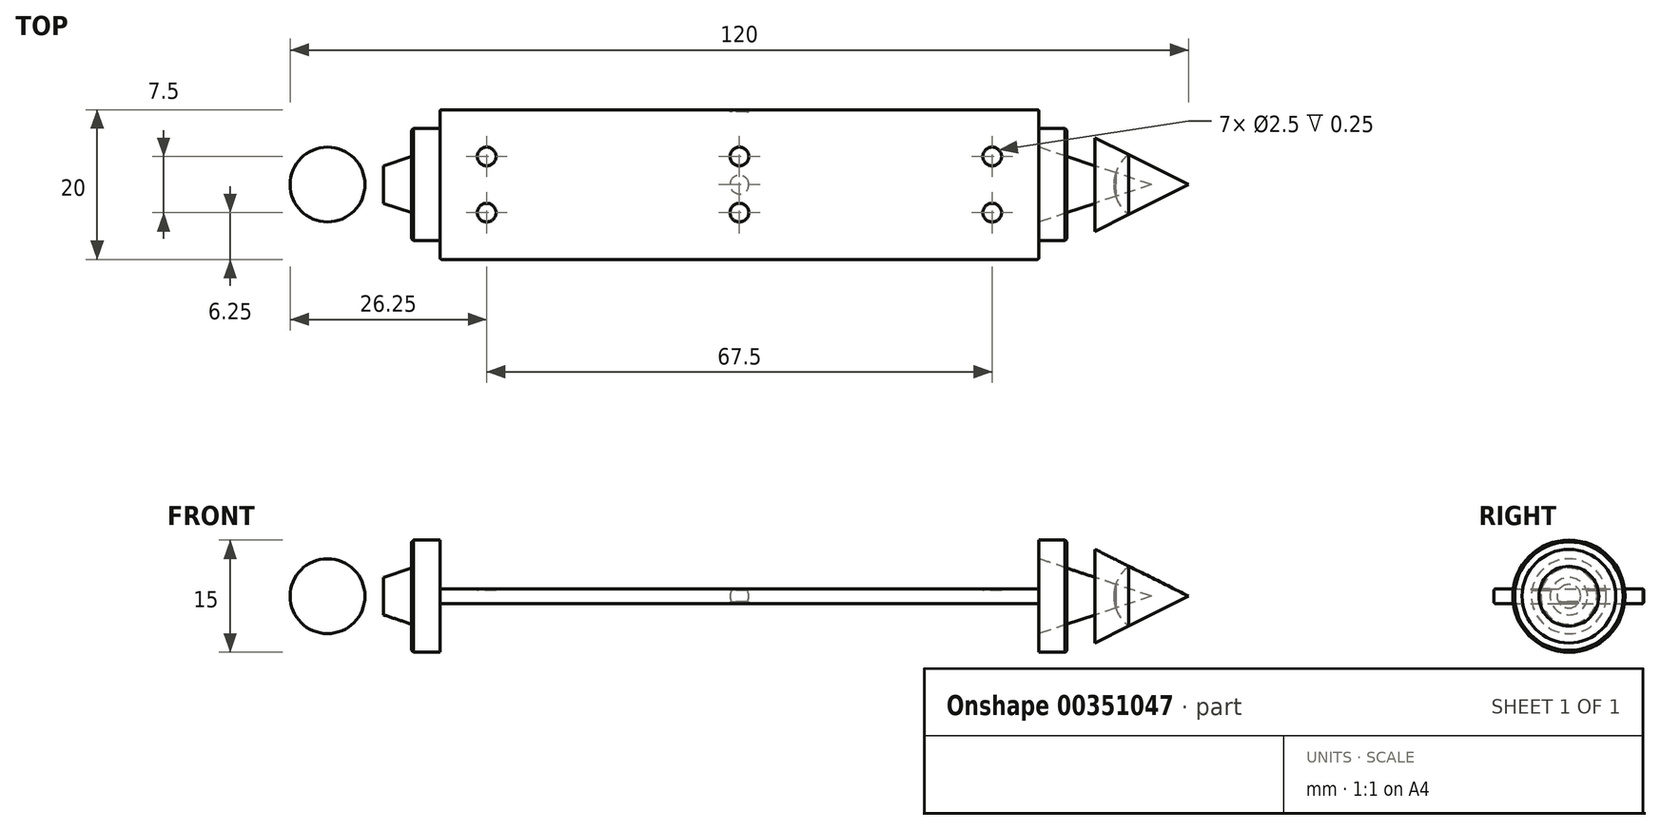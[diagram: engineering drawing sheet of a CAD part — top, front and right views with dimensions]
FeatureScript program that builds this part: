
annotation { "Feature Type Name" : "Feature", "Feature Type Description" : "" }
export const myFeature = defineFeature(function(context is Context, id is Id, definition is map)
    precondition{}
    {
        {
            assignVariable(context, id + "F0", {"name" : "H", "anyValue" : 2});
        }
        {
            assignVariable(context, id + "F1", {"name" : "E", "anyValue" : .25});
        }
        {
            var Q0;
            Q0=qCreatedBy(makeId("Top.planeOp"),FACE);
            var sketch = newSketch(context, id + "F2", { "sketchPlane" : qUnion([Q0])});
            skLineSegment(sketch, "E0.bottom", {"start": v(0, 0) * mm, "end": v(-40, 0) * mm});
            skLineSegment(sketch, "E0.top", {"start": v(0, 10) * mm, "end": v(-40, 10) * mm});
            skLineSegment(sketch, "E0.left", {"start": v(0, 0) * mm, "end": v(0, 10) * mm});
            skLineSegment(sketch, "E0.right", {"start": v(-40, 0) * mm, "end": v(-40, 10) * mm});
            skLineSegment(sketch, "E1.MirrorCS", {"start": v(0, 10) * mm, "end": v(40, 10) * mm});
            skLineSegment(sketch, "E2.MirrorCS", {"start": v(40, 0) * mm, "end": v(40, 10) * mm});
            skLineSegment(sketch, "E3.MirrorCS", {"start": v(0, 0) * mm, "end": v(40, 0) * mm});
            skLineSegment(sketch, "E4.MirrorCS", {"start": v(0, -10) * mm, "end": v(-40, -10) * mm});
            skLineSegment(sketch, "E5.MirrorCS", {"start": v(0, -10) * mm, "end": v(40, -10) * mm});
            skLineSegment(sketch, "E6.MirrorCS", {"start": v(-40, 0) * mm, "end": v(-40, -10) * mm});
            skLineSegment(sketch, "E7.MirrorCS", {"start": v(40, 0) * mm, "end": v(40, -10) * mm});
            skLineSegment(sketch, "E8", {"start": v(40, 0) * mm, "end": v(60, 0) * mm});
            skPoint(sketch, "E9", {"position": v(40, 5) * mm});
            skPoint(sketch, "E10", {"position": v(40, -5) * mm});
            skPoint(sketch, "E11", {"position": v(50, 0) * mm});
            skPoint(sketch, "E12", {"position": v(55, 0) * mm});
            skCircle(sketch, "E13", {"center": v(55, 0) * mm, "radius": 5 * mm});
            skLineSegment(sketch, "E14", {"start": v(55, 0) * mm, "end": v(40, 5) * mm});
            skLineSegment(sketch, "E15", {"start": v(40, -5) * mm, "end": v(55, 0) * mm});
            skLineSegment(sketch, "E16", {"start": v(60, 0) * mm, "end": v(40, 10) * mm});
            skLineSegment(sketch, "E17", {"start": v(60, 0) * mm, "end": v(40, -10) * mm});
            skCircle(sketch, "E18.MirrorC", {"center": v(-55, 0) * mm, "radius": 5 * mm});
            skLineSegment(sketch, "E19.MirrorCS", {"start": v(-55, 0) * mm, "end": v(-40, 5) * mm});
            skLineSegment(sketch, "E20.MirrorCS", {"start": v(-60, 0) * mm, "end": v(-40, 10) * mm});
            skLineSegment(sketch, "E21.MirrorCS", {"start": v(-40, 0) * mm, "end": v(-60, 0) * mm});
            skPoint(sketch, "E22", {"position": v(40, 7.5) * mm});
            skPoint(sketch, "E23", {"position": v(40, -7.5) * mm});
            skPoint(sketch, "E24.oppositeSnap0", {"position": v(47.5, 2.5) * mm});
            skLineSegment(sketch, "E24.bottom", {"start": v(40, 7.5) * mm, "end": v(47.5, 7.5) * mm});
            skLineSegment(sketch, "E24.top", {"start": v(40, -7.5) * mm, "end": v(47.5, -7.5) * mm});
            skLineSegment(sketch, "E24.left", {"start": v(40, 7.5) * mm, "end": v(40, -7.5) * mm});
            skLineSegment(sketch, "E24.right", {"start": v(47.5, 7.5) * mm, "end": v(47.5, -7.5) * mm});
            skLineSegment(sketch, "E25.MirrorCS", {"start": v(-40, 7.5) * mm, "end": v(-47.5, 7.5) * mm});
            skLineSegment(sketch, "E26.MirrorCS", {"start": v(-47.5, 7.5) * mm, "end": v(-47.5, -7.5) * mm});
            skLineSegment(sketch, "E27", {"start": v(43.75, 7.5) * mm, "end": v(43.75, -7.5) * mm});
            skLineSegment(sketch, "E28.MirrorCS", {"start": v(-43.75, 7.5) * mm, "end": v(-43.75, -7.5) * mm});
            skSolve(sketch);
        }
        {
            var Q0;
            Q0=makeQuery(id+"F2.imprint","IMPRINT",FACE,{"disambiguationData":[TD([[makeQuery(id+"F2.imprint","IMPRINT",EDGE,{"derivedFrom":sQuery(id+"F2.wireOp",EDGE,"E0.bottom")}),-1.0]])]});
            var Q1;
            Q1=makeQuery(id+"F2.imprint","IMPRINT",FACE,{"disambiguationData":[TD([[makeQuery(id+"F2.imprint","IMPRINT",EDGE,{"derivedFrom":sQuery(id+"F2.wireOp",EDGE,"E0.left")}),-1.0]])]});
            var Q2;
            Q2=makeQuery(id+"F2.imprint","IMPRINT",FACE,{"disambiguationData":[TD([[makeQuery(id+"F2.imprint","IMPRINT",EDGE,{"derivedFrom":sQuery(id+"F2.wireOp",EDGE,"E0.bottom")}),1.0]])]});
            extrude(context, id + "F3", {"entities" : qUnion([Q0, Q1, Q2]), "depth" : (getVariable(context, 'H') / 2) * mm, "hasSecondDirection" : true, "secondDirectionOppositeDirection" : true, "secondDirectionDepth" : (getVariable(context, 'H') / 2) * mm});
        }
        {
            var Q0;
            Q0=makeQuery(id+"F3.opExtrude","CAP_EDGE",EDGE,{"disambiguationData":[OSD([sQuery(id+"F2.wireOp",EDGE,"E4.MirrorCS"),sQuery(id+"F2.wireOp",EDGE,"E5.MirrorCS")])],"isStart":false});
            var Q1;
            Q1=makeQuery(id+"F3.opExtrude","CAP_EDGE",EDGE,{"disambiguationData":[OSD([sQuery(id+"F2.wireOp",EDGE,"E0.top"),sQuery(id+"F2.wireOp",EDGE,"E1.MirrorCS")])],"isStart":false});
            var Q2;
            Q2=makeQuery(id+"F3.opExtrude","CAP_EDGE",EDGE,{"disambiguationData":[OSD([sQuery(id+"F2.wireOp",EDGE,"E4.MirrorCS"),sQuery(id+"F2.wireOp",EDGE,"E5.MirrorCS")])],"isStart":true});
            var Q3;
            Q3=makeQuery(id+"F3.opExtrude","CAP_EDGE",EDGE,{"disambiguationData":[OSD([sQuery(id+"F2.wireOp",EDGE,"E0.top"),sQuery(id+"F2.wireOp",EDGE,"E1.MirrorCS")])],"isStart":true});
            var Q4;
            Q4=makeQuery(id+"F3.opExtrude","CAP_EDGE",EDGE,{"disambiguationData":[OSD([sQuery(id+"F2.wireOp",EDGE,"E0.right"),sQuery(id+"F2.wireOp",EDGE,"E6.MirrorCS")])],"isStart":true});
            var Q5;
            Q5=makeQuery(id+"F3.opExtrude","SWEPT_EDGE",EDGE,{"disambiguationData":[OSD([sQuery(id+"F2.wireOp",EDGE,"E0.top"),sQuery(id+"F2.wireOp",EDGE,"E0.right")])]});
            var Q6;
            Q6=makeQuery(id+"F3.opExtrude","SWEPT_FACE",FACE,{"disambiguationData":[OSD([sQuery(id+"F2.wireOp",EDGE,"E0.right"),sQuery(id+"F2.wireOp",EDGE,"E6.MirrorCS")])]});
            var Q7;
            Q7=makeQuery(id+"F3.opExtrude","SWEPT_FACE",FACE,{"disambiguationData":[OSD([sQuery(id+"F2.wireOp",EDGE,"E2.MirrorCS"),sQuery(id+"F2.wireOp",EDGE,"E7.MirrorCS")])]});
            fillet(context, id + "F4", {"entities" : qUnion([Q0, Q1, Q2, Q3, Q4, Q5, Q6, Q7]), "radius" : (getVariable(context, 'E')) * mm, "tangentPropagation" : true, "allowEdgeOverflow" : false});
        }
        {
            var Q0;
            Q0=makeQuery(id+"F3.opExtrude","CAP_FACE",FACE,{"disambiguationData":[OSD([sQuery(id+"F2.wireOp",EDGE,"E0.top"),sQuery(id+"F2.wireOp",EDGE,"E0.right"),sQuery(id+"F2.wireOp",EDGE,"E1.MirrorCS"),sQuery(id+"F2.wireOp",EDGE,"E2.MirrorCS"),sQuery(id+"F2.wireOp",EDGE,"E4.MirrorCS"),sQuery(id+"F2.wireOp",EDGE,"E5.MirrorCS"),sQuery(id+"F2.wireOp",EDGE,"E6.MirrorCS"),sQuery(id+"F2.wireOp",EDGE,"E7.MirrorCS")])],"isStart":false});
            var sketch = newSketch(context, id + "F5", { "sketchPlane" : qUnion([Q0])});
            skLineSegment(sketch, "E29.bottom", {"start": v(-33.75, 3.75) * mm, "end": v(33.75, 3.75) * mm});
            skLineSegment(sketch, "E29.top", {"start": v(-33.75, -3.75) * mm, "end": v(33.75, -3.75) * mm});
            skLineSegment(sketch, "E29.left", {"start": v(-33.75, 3.75) * mm, "end": v(-33.75, -3.75) * mm});
            skLineSegment(sketch, "E29.right", {"start": v(33.75, 3.75) * mm, "end": v(33.75, -3.75) * mm});
            skPoint(sketch, "E29.middle", {"position": v(0, 0) * mm});
            skLineSegment(sketch, "E30", {"start": v(-33.75, 0) * mm, "end": v(33.75, 0) * mm});
            skLineSegment(sketch, "E31", {"start": v(0, 3.75) * mm, "end": v(0, -3.75) * mm});
            skCircle(sketch, "E32", {"center": v(-33.75, 0) * mm, "radius": 1.25 * mm});
            skCircle(sketch, "E33", {"center": v(-33.75, 3.75) * mm, "radius": 1.25 * mm});
            skCircle(sketch, "E34", {"center": v(0, 3.75) * mm, "radius": 1.25 * mm});
            skCircle(sketch, "E35", {"center": v(0, 0) * mm, "radius": 1.25 * mm});
            skCircle(sketch, "E36.MirrorC", {"center": v(33.75, 3.75) * mm, "radius": 1.25 * mm});
            skCircle(sketch, "E37.MirrorC", {"center": v(33.75, 0) * mm, "radius": 1.25 * mm});
            skCircle(sketch, "E38.MirrorC", {"center": v(0, -3.75) * mm, "radius": 1.25 * mm});
            skCircle(sketch, "E39.MirrorC", {"center": v(-33.75, -3.75) * mm, "radius": 1.25 * mm});
            skCircle(sketch, "E40.MirrorC", {"center": v(33.75, -3.75) * mm, "radius": 1.25 * mm});
            skSolve(sketch);
        }
        {
            var Q0;
            Q0=makeQuery(id+"F3.opExtrude","CAP_FACE",FACE,{"disambiguationData":[OSD([sQuery(id+"F2.wireOp",EDGE,"E0.top"),sQuery(id+"F2.wireOp",EDGE,"E0.right"),sQuery(id+"F2.wireOp",EDGE,"E1.MirrorCS"),sQuery(id+"F2.wireOp",EDGE,"E2.MirrorCS"),sQuery(id+"F2.wireOp",EDGE,"E4.MirrorCS"),sQuery(id+"F2.wireOp",EDGE,"E5.MirrorCS"),sQuery(id+"F2.wireOp",EDGE,"E6.MirrorCS"),sQuery(id+"F2.wireOp",EDGE,"E7.MirrorCS")])],"isStart":true});
            var sketch = newSketch(context, id + "F6", { "sketchPlane" : qUnion([Q0])});
            skLineSegment(sketch, "E41.bottom", {"start": v(-33.75, 3.75) * mm, "end": v(33.75, 3.75) * mm});
            skLineSegment(sketch, "E41.top", {"start": v(-33.75, -3.75) * mm, "end": v(33.75, -3.75) * mm});
            skLineSegment(sketch, "E41.left", {"start": v(-33.75, 3.75) * mm, "end": v(-33.75, -3.75) * mm});
            skLineSegment(sketch, "E41.right", {"start": v(33.75, 3.75) * mm, "end": v(33.75, -3.75) * mm});
            skPoint(sketch, "E41.middle", {"position": v(0, 0) * mm});
            skLineSegment(sketch, "E42", {"start": v(-33.75, 0) * mm, "end": v(33.75, 0) * mm});
            skLineSegment(sketch, "E43", {"start": v(0, 3.75) * mm, "end": v(0, -3.75) * mm});
            skCircle(sketch, "E44", {"center": v(-33.75, 0) * mm, "radius": 1.25 * mm});
            skCircle(sketch, "E45", {"center": v(-33.75, 3.75) * mm, "radius": 1.25 * mm});
            skCircle(sketch, "E46", {"center": v(0, 3.75) * mm, "radius": 1.25 * mm});
            skCircle(sketch, "E47", {"center": v(0, 0) * mm, "radius": 1.25 * mm});
            skCircle(sketch, "E48.MirrorC", {"center": v(33.75, -3.75) * mm, "radius": 1.25 * mm});
            skCircle(sketch, "E49.MirrorC", {"center": v(33.75, 0) * mm, "radius": 1.25 * mm});
            skCircle(sketch, "E50.MirrorC", {"center": v(0, -3.75) * mm, "radius": 1.25 * mm});
            skCircle(sketch, "E51.MirrorC", {"center": v(-33.75, -3.75) * mm, "radius": 1.25 * mm});
            skCircle(sketch, "E52.MirrorC", {"center": v(33.75, 3.75) * mm, "radius": 1.25 * mm});
            skSolve(sketch);
        }
        {
            var Q0;
            Q0=makeQuery(id+"F3.opExtrude","SWEPT_FACE",FACE,{"disambiguationData":[OSD([sQuery(id+"F2.wireOp",EDGE,"E4.MirrorCS"),sQuery(id+"F2.wireOp",EDGE,"E5.MirrorCS")])]});
            var sketch = newSketch(context, id + "F7", { "sketchPlane" : qUnion([Q0])});
            skLineSegment(sketch, "E53.bottom", {"start": v(-33.75, 3.75) * mm, "end": v(33.75, 3.75) * mm});
            skLineSegment(sketch, "E53.top", {"start": v(-33.75, -3.75) * mm, "end": v(33.75, -3.75) * mm});
            skLineSegment(sketch, "E53.left", {"start": v(-33.75, 3.75) * mm, "end": v(-33.75, -3.75) * mm});
            skLineSegment(sketch, "E53.right", {"start": v(33.75, 3.75) * mm, "end": v(33.75, -3.75) * mm});
            skPoint(sketch, "E53.middle", {"position": v(0, 0) * mm});
            skLineSegment(sketch, "E54", {"start": v(-33.75, 0) * mm, "end": v(33.75, 0) * mm});
            skLineSegment(sketch, "E55", {"start": v(0, 3.75) * mm, "end": v(0, -3.75) * mm});
            skCircle(sketch, "E56", {"center": v(-33.75, 0) * mm, "radius": 1.25 * mm});
            skCircle(sketch, "E57", {"center": v(-33.75, 3.75) * mm, "radius": 1.25 * mm});
            skCircle(sketch, "E58", {"center": v(0, 3.75) * mm, "radius": 1.25 * mm});
            skCircle(sketch, "E59", {"center": v(0, 0) * mm, "radius": 1.25 * mm});
            skCircle(sketch, "E60.MirrorC", {"center": v(33.75, 3.75) * mm, "radius": 1.25 * mm});
            skCircle(sketch, "E61.MirrorC", {"center": v(33.75, 0) * mm, "radius": 1.25 * mm});
            skCircle(sketch, "E62.MirrorC", {"center": v(0, -3.75) * mm, "radius": 1.25 * mm});
            skCircle(sketch, "E63.MirrorC", {"center": v(-33.75, -3.75) * mm, "radius": 1.25 * mm});
            skCircle(sketch, "E64.MirrorC", {"center": v(33.75, -3.75) * mm, "radius": 1.25 * mm});
            skSolve(sketch);
        }
        {
            var Q0;
            Q0=makeQuery(id+"F3.opExtrude","SWEPT_FACE",FACE,{"disambiguationData":[OSD([sQuery(id+"F2.wireOp",EDGE,"E0.top"),sQuery(id+"F2.wireOp",EDGE,"E1.MirrorCS")])]});
            var sketch = newSketch(context, id + "F8", { "sketchPlane" : qUnion([Q0])});
            skLineSegment(sketch, "E65.bottom", {"start": v(-33.75, 3.75) * mm, "end": v(33.75, 3.75) * mm});
            skLineSegment(sketch, "E65.top", {"start": v(-33.75, -3.75) * mm, "end": v(33.75, -3.75) * mm});
            skLineSegment(sketch, "E65.left", {"start": v(-33.75, 3.75) * mm, "end": v(-33.75, -3.75) * mm});
            skLineSegment(sketch, "E65.right", {"start": v(33.75, 3.75) * mm, "end": v(33.75, -3.75) * mm});
            skPoint(sketch, "E65.middle", {"position": v(0, 0) * mm});
            skLineSegment(sketch, "E66", {"start": v(-33.75, 0) * mm, "end": v(33.75, 0) * mm});
            skLineSegment(sketch, "E67", {"start": v(0, 3.75) * mm, "end": v(0, -3.75) * mm});
            skCircle(sketch, "E68", {"center": v(-33.75, 0) * mm, "radius": 1.25 * mm});
            skCircle(sketch, "E69", {"center": v(-33.75, 3.75) * mm, "radius": 1.25 * mm});
            skCircle(sketch, "E70", {"center": v(0, 3.75) * mm, "radius": 1.25 * mm});
            skCircle(sketch, "E71", {"center": v(0, 0) * mm, "radius": 1.25 * mm});
            skCircle(sketch, "E72.MirrorC", {"center": v(33.75, -3.75) * mm, "radius": 1.25 * mm});
            skCircle(sketch, "E73.MirrorC", {"center": v(33.75, 0) * mm, "radius": 1.25 * mm});
            skCircle(sketch, "E74.MirrorC", {"center": v(0, -3.75) * mm, "radius": 1.25 * mm});
            skCircle(sketch, "E75.MirrorC", {"center": v(-33.75, -3.75) * mm, "radius": 1.25 * mm});
            skCircle(sketch, "E76.MirrorC", {"center": v(33.75, 3.75) * mm, "radius": 1.25 * mm});
            skSolve(sketch);
        }
        {
            var Q0;
            {var subQ0=sQuery(id+"F5.wireOp",EDGE,"E29.bottom");var subQ1=makeQuery(id+"F5.imprint","INTERSECT",VERTEX,{"derivedFrom":[subQ0,sQuery(id+"F5.wireOp",EDGE,"E31")]});Q0=makeQuery(id+"F5.imprint","IMPRINT",FACE,{"disambiguationData":[TD([[makeQuery(id+"F5.imprint","IMPRINT",EDGE,{"disambiguationData":[TD([[subQ1,1.0]])],"derivedFrom":subQ0}),1.0]])]});}
            var Q1;
            {var subQ0=sQuery(id+"F5.wireOp",EDGE,"E31");var subQ1=sQuery(id+"F5.wireOp",EDGE,"E29.bottom");var subQ2=makeQuery(id+"F5.imprint","INTERSECT",VERTEX,{"derivedFrom":[subQ1,subQ0]});Q1=makeQuery(id+"F5.imprint","IMPRINT",FACE,{"disambiguationData":[TD([[makeQuery(id+"F5.imprint","IMPRINT",EDGE,{"disambiguationData":[TD([[subQ2,-1.0]])],"derivedFrom":subQ1}),-1.0]])]});}
            var Q2;
            {var subQ0=sQuery(id+"F5.wireOp",EDGE,"E31");var subQ1=sQuery(id+"F5.wireOp",EDGE,"E29.bottom");var subQ2=makeQuery(id+"F5.imprint","INTERSECT",VERTEX,{"derivedFrom":[subQ1,subQ0]});Q2=makeQuery(id+"F5.imprint","IMPRINT",FACE,{"disambiguationData":[TD([[makeQuery(id+"F5.imprint","IMPRINT",EDGE,{"disambiguationData":[TD([[subQ2,1.0]])],"derivedFrom":subQ1}),-1.0]])]});}
            var Q3;
            {var subQ0=sQuery(id+"F5.wireOp",EDGE,"E31");var subQ1=sQuery(id+"F5.wireOp",EDGE,"E29.top");var subQ2=makeQuery(id+"F5.imprint","INTERSECT",VERTEX,{"derivedFrom":[subQ1,subQ0]});Q3=makeQuery(id+"F5.imprint","IMPRINT",FACE,{"disambiguationData":[TD([[makeQuery(id+"F5.imprint","IMPRINT",EDGE,{"disambiguationData":[TD([[subQ2,-1.0]])],"derivedFrom":subQ1}),1.0]])]});}
            var Q4;
            {var subQ0=sQuery(id+"F5.wireOp",EDGE,"E31");var subQ1=sQuery(id+"F5.wireOp",EDGE,"E29.top");var subQ2=makeQuery(id+"F5.imprint","INTERSECT",VERTEX,{"derivedFrom":[subQ1,subQ0]});Q4=makeQuery(id+"F5.imprint","IMPRINT",FACE,{"disambiguationData":[TD([[makeQuery(id+"F5.imprint","IMPRINT",EDGE,{"disambiguationData":[TD([[subQ2,1.0]])],"derivedFrom":subQ1}),1.0]])]});}
            var Q5;
            {var subQ0=sQuery(id+"F5.wireOp",EDGE,"E29.top");var subQ1=makeQuery(id+"F5.imprint","INTERSECT",VERTEX,{"derivedFrom":[subQ0,sQuery(id+"F5.wireOp",EDGE,"E31")]});Q5=makeQuery(id+"F5.imprint","IMPRINT",FACE,{"disambiguationData":[TD([[makeQuery(id+"F5.imprint","IMPRINT",EDGE,{"disambiguationData":[TD([[subQ1,1.0]])],"derivedFrom":subQ0}),-1.0]])]});}
            var Q6;
            {var subQ0=sQuery(id+"F5.wireOp",EDGE,"E29.right");var subQ1=sQuery(id+"F5.wireOp",EDGE,"E29.bottom");var subQ2=makeQuery(id+"F5.imprint","INTERSECT",VERTEX,{"derivedFrom":[subQ1,subQ0]});Q6=makeQuery(id+"F5.imprint","IMPRINT",FACE,{"disambiguationData":[TD([[makeQuery(id+"F5.imprint","IMPRINT",EDGE,{"disambiguationData":[TD([[subQ2,1.0]])],"derivedFrom":subQ1}),1.0]])]});}
            var Q7;
            {var subQ0=sQuery(id+"F5.wireOp",EDGE,"E29.right");var subQ1=sQuery(id+"F5.wireOp",EDGE,"E29.top");var subQ2=makeQuery(id+"F5.imprint","INTERSECT",VERTEX,{"derivedFrom":[subQ1,subQ0]});Q7=makeQuery(id+"F5.imprint","IMPRINT",FACE,{"disambiguationData":[TD([[makeQuery(id+"F5.imprint","IMPRINT",EDGE,{"disambiguationData":[TD([[subQ2,1.0]])],"derivedFrom":subQ1}),-1.0]])]});}
            var Q8;
            {var subQ0=sQuery(id+"F5.wireOp",EDGE,"E29.right");var subQ1=sQuery(id+"F5.wireOp",EDGE,"E29.top");var subQ2=makeQuery(id+"F5.imprint","INTERSECT",VERTEX,{"derivedFrom":[subQ1,subQ0]});Q8=makeQuery(id+"F5.imprint","IMPRINT",FACE,{"disambiguationData":[TD([[makeQuery(id+"F5.imprint","IMPRINT",EDGE,{"disambiguationData":[TD([[subQ2,1.0]])],"derivedFrom":subQ1}),1.0]])]});}
            var Q9;
            {var subQ0=sQuery(id+"F5.wireOp",EDGE,"E29.right");var subQ1=sQuery(id+"F5.wireOp",EDGE,"E29.bottom");var subQ2=makeQuery(id+"F5.imprint","INTERSECT",VERTEX,{"derivedFrom":[subQ1,subQ0]});Q9=makeQuery(id+"F5.imprint","IMPRINT",FACE,{"disambiguationData":[TD([[makeQuery(id+"F5.imprint","IMPRINT",EDGE,{"disambiguationData":[TD([[subQ2,1.0]])],"derivedFrom":subQ1}),-1.0]])]});}
            var Q10;
            {var subQ0=sQuery(id+"F5.wireOp",EDGE,"E29.left");var subQ1=sQuery(id+"F5.wireOp",EDGE,"E29.top");var subQ2=makeQuery(id+"F5.imprint","INTERSECT",VERTEX,{"derivedFrom":[subQ1,subQ0]});Q10=makeQuery(id+"F5.imprint","IMPRINT",FACE,{"disambiguationData":[TD([[makeQuery(id+"F5.imprint","IMPRINT",EDGE,{"disambiguationData":[TD([[subQ2,-1.0]])],"derivedFrom":subQ1}),-1.0]])]});}
            var Q11;
            {var subQ0=sQuery(id+"F5.wireOp",EDGE,"E29.left");var subQ1=sQuery(id+"F5.wireOp",EDGE,"E29.top");var subQ2=makeQuery(id+"F5.imprint","INTERSECT",VERTEX,{"derivedFrom":[subQ1,subQ0]});Q11=makeQuery(id+"F5.imprint","IMPRINT",FACE,{"disambiguationData":[TD([[makeQuery(id+"F5.imprint","IMPRINT",EDGE,{"disambiguationData":[TD([[subQ2,-1.0]])],"derivedFrom":subQ1}),1.0]])]});}
            var Q12;
            {var subQ0=sQuery(id+"F5.wireOp",EDGE,"E29.left");var subQ1=sQuery(id+"F5.wireOp",EDGE,"E29.bottom");var subQ2=makeQuery(id+"F5.imprint","INTERSECT",VERTEX,{"derivedFrom":[subQ1,subQ0]});Q12=makeQuery(id+"F5.imprint","IMPRINT",FACE,{"disambiguationData":[TD([[makeQuery(id+"F5.imprint","IMPRINT",EDGE,{"disambiguationData":[TD([[subQ2,-1.0]])],"derivedFrom":subQ1}),1.0]])]});}
            var Q13;
            {var subQ0=sQuery(id+"F5.wireOp",EDGE,"E29.left");var subQ1=sQuery(id+"F5.wireOp",EDGE,"E29.bottom");var subQ2=makeQuery(id+"F5.imprint","INTERSECT",VERTEX,{"derivedFrom":[subQ1,subQ0]});Q13=makeQuery(id+"F5.imprint","IMPRINT",FACE,{"disambiguationData":[TD([[makeQuery(id+"F5.imprint","IMPRINT",EDGE,{"disambiguationData":[TD([[subQ2,-1.0]])],"derivedFrom":subQ1}),-1.0]])]});}
            extrude(context, id + "F9", {"entities" : qUnion([Q0, Q1, Q2, Q3, Q4, Q5, Q6, Q7, Q8, Q9, Q10, Q11, Q12, Q13]), "operationType" : NewBodyOperationType.REMOVE, "oppositeDirection" : true, "depth" : (getVariable(context, 'E')) * mm});
        }
        {
            var Q0;
            {var subQ0=sQuery(id+"F6.wireOp",EDGE,"E47");var subQ1=sQuery(id+"F6.wireOp",EDGE,"E42");var subQ2=makeQuery(id+"F6.imprint","INTERSECT",VERTEX,{"disambiguationData":[OD(0.0)],"derivedFrom":[subQ1,subQ0]});Q0=makeQuery(id+"F6.imprint","IMPRINT",FACE,{"disambiguationData":[TD([[makeQuery(id+"F6.imprint","IMPRINT",EDGE,{"disambiguationData":[TD([[subQ2,-1.0]])],"derivedFrom":subQ1}),1.0]])]});}
            var Q1;
            {var subQ0=sQuery(id+"F6.wireOp",EDGE,"E47");var subQ1=sQuery(id+"F6.wireOp",EDGE,"E42");var subQ2=makeQuery(id+"F6.imprint","INTERSECT",VERTEX,{"disambiguationData":[OD(0.0)],"derivedFrom":[subQ1,subQ0]});Q1=makeQuery(id+"F6.imprint","IMPRINT",FACE,{"disambiguationData":[TD([[makeQuery(id+"F6.imprint","IMPRINT",EDGE,{"disambiguationData":[TD([[subQ2,-1.0]])],"derivedFrom":subQ1}),-1.0]])]});}
            var Q2;
            {var subQ0=sQuery(id+"F6.wireOp",EDGE,"E43");var subQ1=sQuery(id+"F6.wireOp",EDGE,"E42");var subQ2=makeQuery(id+"F6.imprint","INTERSECT",VERTEX,{"derivedFrom":[subQ1,subQ0]});Q2=makeQuery(id+"F6.imprint","IMPRINT",FACE,{"disambiguationData":[TD([[makeQuery(id+"F6.imprint","IMPRINT",EDGE,{"disambiguationData":[TD([[subQ2,-1.0]])],"derivedFrom":subQ1}),-1.0]])]});}
            var Q3;
            {var subQ0=sQuery(id+"F6.wireOp",EDGE,"E43");var subQ1=sQuery(id+"F6.wireOp",EDGE,"E42");var subQ2=makeQuery(id+"F6.imprint","INTERSECT",VERTEX,{"derivedFrom":[subQ1,subQ0]});Q3=makeQuery(id+"F6.imprint","IMPRINT",FACE,{"disambiguationData":[TD([[makeQuery(id+"F6.imprint","IMPRINT",EDGE,{"disambiguationData":[TD([[subQ2,-1.0]])],"derivedFrom":subQ1}),1.0]])]});}
            extrude(context, id + "F10", {"entities" : qUnion([Q0, Q1, Q2, Q3]), "operationType" : NewBodyOperationType.REMOVE, "oppositeDirection" : true, "depth" : (getVariable(context, 'E')) * mm});
        }
        {
            var Q0;
            {var subQ0=sQuery(id+"F7.wireOp",EDGE,"E53.right");var subQ1=sQuery(id+"F7.wireOp",EDGE,"E53.top");var subQ2=makeQuery(id+"F7.imprint","INTERSECT",VERTEX,{"derivedFrom":[subQ1,subQ0]});Q0=makeQuery(id+"F7.imprint","IMPRINT",FACE,{"disambiguationData":[TD([[makeQuery(id+"F7.imprint","IMPRINT",EDGE,{"disambiguationData":[TD([[subQ2,1.0]])],"derivedFrom":subQ1}),-1.0]])]});}
            var Q1;
            {var subQ0=sQuery(id+"F7.wireOp",EDGE,"E53.right");var subQ1=sQuery(id+"F7.wireOp",EDGE,"E53.top");var subQ2=makeQuery(id+"F7.imprint","INTERSECT",VERTEX,{"derivedFrom":[subQ1,subQ0]});Q1=makeQuery(id+"F7.imprint","IMPRINT",FACE,{"disambiguationData":[TD([[makeQuery(id+"F7.imprint","IMPRINT",EDGE,{"disambiguationData":[TD([[subQ2,1.0]])],"derivedFrom":subQ1}),1.0]])]});}
            var Q2;
            {var subQ0=sQuery(id+"F7.wireOp",EDGE,"E53.right");var subQ1=sQuery(id+"F7.wireOp",EDGE,"E53.bottom");var subQ2=makeQuery(id+"F7.imprint","INTERSECT",VERTEX,{"derivedFrom":[subQ1,subQ0]});Q2=makeQuery(id+"F7.imprint","IMPRINT",FACE,{"disambiguationData":[TD([[makeQuery(id+"F7.imprint","IMPRINT",EDGE,{"disambiguationData":[TD([[subQ2,1.0]])],"derivedFrom":subQ1}),1.0]])]});}
            var Q3;
            {var subQ0=sQuery(id+"F7.wireOp",EDGE,"E53.right");var subQ1=sQuery(id+"F7.wireOp",EDGE,"E53.bottom");var subQ2=makeQuery(id+"F7.imprint","INTERSECT",VERTEX,{"derivedFrom":[subQ1,subQ0]});Q3=makeQuery(id+"F7.imprint","IMPRINT",FACE,{"disambiguationData":[TD([[makeQuery(id+"F7.imprint","IMPRINT",EDGE,{"disambiguationData":[TD([[subQ2,1.0]])],"derivedFrom":subQ1}),-1.0]])]});}
            var Q4;
            {var subQ0=sQuery(id+"F7.wireOp",EDGE,"E53.left");var subQ1=sQuery(id+"F7.wireOp",EDGE,"E53.top");var subQ2=makeQuery(id+"F7.imprint","INTERSECT",VERTEX,{"derivedFrom":[subQ1,subQ0]});Q4=makeQuery(id+"F7.imprint","IMPRINT",FACE,{"disambiguationData":[TD([[makeQuery(id+"F7.imprint","IMPRINT",EDGE,{"disambiguationData":[TD([[subQ2,-1.0]])],"derivedFrom":subQ1}),-1.0]])]});}
            var Q5;
            {var subQ0=sQuery(id+"F7.wireOp",EDGE,"E53.left");var subQ1=sQuery(id+"F7.wireOp",EDGE,"E53.bottom");var subQ2=makeQuery(id+"F7.imprint","INTERSECT",VERTEX,{"derivedFrom":[subQ1,subQ0]});Q5=makeQuery(id+"F7.imprint","IMPRINT",FACE,{"disambiguationData":[TD([[makeQuery(id+"F7.imprint","IMPRINT",EDGE,{"disambiguationData":[TD([[subQ2,-1.0]])],"derivedFrom":subQ1}),1.0]])]});}
            var Q6;
            {var subQ0=sQuery(id+"F7.wireOp",EDGE,"E53.left");var subQ1=sQuery(id+"F7.wireOp",EDGE,"E53.bottom");var subQ2=makeQuery(id+"F7.imprint","INTERSECT",VERTEX,{"derivedFrom":[subQ1,subQ0]});Q6=makeQuery(id+"F7.imprint","IMPRINT",FACE,{"disambiguationData":[TD([[makeQuery(id+"F7.imprint","IMPRINT",EDGE,{"disambiguationData":[TD([[subQ2,-1.0]])],"derivedFrom":subQ1}),-1.0]])]});}
            var Q7;
            {var subQ0=sQuery(id+"F7.wireOp",EDGE,"E53.left");var subQ1=sQuery(id+"F7.wireOp",EDGE,"E53.top");var subQ2=makeQuery(id+"F7.imprint","INTERSECT",VERTEX,{"derivedFrom":[subQ1,subQ0]});Q7=makeQuery(id+"F7.imprint","IMPRINT",FACE,{"disambiguationData":[TD([[makeQuery(id+"F7.imprint","IMPRINT",EDGE,{"disambiguationData":[TD([[subQ2,-1.0]])],"derivedFrom":subQ1}),1.0]])]});}
            extrude(context, id + "F11", {"entities" : qUnion([Q0, Q1, Q2, Q3, Q4, Q5, Q6, Q7]), "operationType" : NewBodyOperationType.REMOVE, "oppositeDirection" : true, "depth" : (getVariable(context, 'E')) * mm});
        }
        {
            var Q0;
            {var subQ0=sQuery(id+"F8.wireOp",EDGE,"E65.right");var subQ1=sQuery(id+"F8.wireOp",EDGE,"E65.top");var subQ2=makeQuery(id+"F8.imprint","INTERSECT",VERTEX,{"derivedFrom":[subQ1,subQ0]});Q0=makeQuery(id+"F8.imprint","IMPRINT",FACE,{"disambiguationData":[TD([[makeQuery(id+"F8.imprint","IMPRINT",EDGE,{"disambiguationData":[TD([[subQ2,1.0]])],"derivedFrom":subQ1}),-1.0]])]});}
            var Q1;
            {var subQ0=sQuery(id+"F8.wireOp",EDGE,"E65.right");var subQ1=sQuery(id+"F8.wireOp",EDGE,"E65.top");var subQ2=makeQuery(id+"F8.imprint","INTERSECT",VERTEX,{"derivedFrom":[subQ1,subQ0]});Q1=makeQuery(id+"F8.imprint","IMPRINT",FACE,{"disambiguationData":[TD([[makeQuery(id+"F8.imprint","IMPRINT",EDGE,{"disambiguationData":[TD([[subQ2,1.0]])],"derivedFrom":subQ1}),1.0]])]});}
            var Q2;
            {var subQ0=sQuery(id+"F8.wireOp",EDGE,"E71");var subQ1=sQuery(id+"F8.wireOp",EDGE,"E66");var subQ2=makeQuery(id+"F8.imprint","INTERSECT",VERTEX,{"disambiguationData":[OD(0.0)],"derivedFrom":[subQ1,subQ0]});Q2=makeQuery(id+"F8.imprint","IMPRINT",FACE,{"disambiguationData":[TD([[makeQuery(id+"F8.imprint","IMPRINT",EDGE,{"disambiguationData":[TD([[subQ2,-1.0]])],"derivedFrom":subQ1}),1.0]])]});}
            var Q3;
            {var subQ0=sQuery(id+"F8.wireOp",EDGE,"E71");var subQ1=sQuery(id+"F8.wireOp",EDGE,"E66");var subQ2=makeQuery(id+"F8.imprint","INTERSECT",VERTEX,{"disambiguationData":[OD(0.0)],"derivedFrom":[subQ1,subQ0]});Q3=makeQuery(id+"F8.imprint","IMPRINT",FACE,{"disambiguationData":[TD([[makeQuery(id+"F8.imprint","IMPRINT",EDGE,{"disambiguationData":[TD([[subQ2,-1.0]])],"derivedFrom":subQ1}),-1.0]])]});}
            var Q4;
            {var subQ0=sQuery(id+"F8.wireOp",EDGE,"E67");var subQ1=sQuery(id+"F8.wireOp",EDGE,"E66");var subQ2=makeQuery(id+"F8.imprint","INTERSECT",VERTEX,{"derivedFrom":[subQ1,subQ0]});Q4=makeQuery(id+"F8.imprint","IMPRINT",FACE,{"disambiguationData":[TD([[makeQuery(id+"F8.imprint","IMPRINT",EDGE,{"disambiguationData":[TD([[subQ2,-1.0]])],"derivedFrom":subQ1}),-1.0]])]});}
            var Q5;
            {var subQ0=sQuery(id+"F8.wireOp",EDGE,"E67");var subQ1=sQuery(id+"F8.wireOp",EDGE,"E66");var subQ2=makeQuery(id+"F8.imprint","INTERSECT",VERTEX,{"derivedFrom":[subQ1,subQ0]});Q5=makeQuery(id+"F8.imprint","IMPRINT",FACE,{"disambiguationData":[TD([[makeQuery(id+"F8.imprint","IMPRINT",EDGE,{"disambiguationData":[TD([[subQ2,-1.0]])],"derivedFrom":subQ1}),1.0]])]});}
            var Q6;
            {var subQ0=sQuery(id+"F8.wireOp",EDGE,"E65.left");var subQ1=sQuery(id+"F8.wireOp",EDGE,"E65.bottom");var subQ2=makeQuery(id+"F8.imprint","INTERSECT",VERTEX,{"derivedFrom":[subQ1,subQ0]});Q6=makeQuery(id+"F8.imprint","IMPRINT",FACE,{"disambiguationData":[TD([[makeQuery(id+"F8.imprint","IMPRINT",EDGE,{"disambiguationData":[TD([[subQ2,-1.0]])],"derivedFrom":subQ1}),-1.0]])]});}
            var Q7;
            {var subQ0=sQuery(id+"F8.wireOp",EDGE,"E65.left");var subQ1=sQuery(id+"F8.wireOp",EDGE,"E65.bottom");var subQ2=makeQuery(id+"F8.imprint","INTERSECT",VERTEX,{"derivedFrom":[subQ1,subQ0]});Q7=makeQuery(id+"F8.imprint","IMPRINT",FACE,{"disambiguationData":[TD([[makeQuery(id+"F8.imprint","IMPRINT",EDGE,{"disambiguationData":[TD([[subQ2,-1.0]])],"derivedFrom":subQ1}),1.0]])]});}
            extrude(context, id + "F12", {"entities" : qUnion([Q0, Q1, Q2, Q3, Q4, Q5, Q6, Q7]), "operationType" : NewBodyOperationType.REMOVE, "oppositeDirection" : true, "depth" : (getVariable(context, 'E')) * mm});
        }
        {
            var Q0;
            {var subQ0=sQuery(id+"F2.wireOp",EDGE,"E8");var subQ5=sQuery(id+"F2.wireOp",EDGE,"E13");var subQ6=makeQuery(id+"F2.imprint","INTERSECT",VERTEX,{"derivedFrom":[subQ0,subQ5]});Q0=makeQuery(id+"F2.imprint","IMPRINT",FACE,{"disambiguationData":[TD([[makeQuery(id+"F2.imprint","IMPRINT",EDGE,{"disambiguationData":[TD([[subQ6,1.0]])],"derivedFrom":subQ5}),-1.0]])]});}
            var Q1;
            {var subQ1=sQuery(id+"F2.wireOp",EDGE,"E8");var subQ3=sQuery(id+"F2.wireOp",EDGE,"E13");var subQ4=makeQuery(id+"F2.imprint","INTERSECT",VERTEX,{"derivedFrom":[subQ1,subQ3]});Q1=makeQuery(id+"F2.imprint","IMPRINT",FACE,{"disambiguationData":[TD([[makeQuery(id+"F2.imprint","IMPRINT",EDGE,{"disambiguationData":[TD([[subQ4,1.0]])],"derivedFrom":subQ3}),1.0]])]});}
            var Q2;
            {var subQ0=sQuery(id+"F2.wireOp",EDGE,"E16");var subQ1=sQuery(id+"F2.wireOp",EDGE,"E13");var subQ6=makeQuery(id+"F2.imprint","INTERSECT",VERTEX,{"derivedFrom":[subQ1,subQ0]});Q2=makeQuery(id+"F2.imprint","IMPRINT",FACE,{"disambiguationData":[TD([[makeQuery(id+"F2.imprint","IMPRINT",EDGE,{"disambiguationData":[TD([[subQ6,-1.0]])],"derivedFrom":subQ1}),1.0]])]});}
            var Q3;
            {var subQ0=sQuery(id+"F2.wireOp",EDGE,"E24.left");var subQ5=sQuery(id+"F2.wireOp",EDGE,"E14");var subQ6=makeQuery(id+"F2.imprint","INTERSECT",VERTEX,{"derivedFrom":[subQ5,subQ0]});Q3=makeQuery(id+"F2.imprint","IMPRINT",FACE,{"disambiguationData":[TD([[makeQuery(id+"F2.imprint","IMPRINT",EDGE,{"disambiguationData":[TD([[subQ6,1.0]])],"derivedFrom":subQ5}),1.0]])]});}
            var Q4;
            {var subQ0=sQuery(id+"F2.wireOp",EDGE,"E24.left");var subQ5=sQuery(id+"F2.wireOp",EDGE,"E14");var subQ6=makeQuery(id+"F2.imprint","INTERSECT",VERTEX,{"derivedFrom":[subQ5,subQ0]});Q4=makeQuery(id+"F2.imprint","IMPRINT",FACE,{"disambiguationData":[TD([[makeQuery(id+"F2.imprint","IMPRINT",EDGE,{"disambiguationData":[TD([[subQ6,1.0]])],"derivedFrom":subQ5}),-1.0]])]});}
            var Q5;
            {var subQ0=sQuery(id+"F2.wireOp",EDGE,"E27");var subQ1=sQuery(id+"F2.wireOp",EDGE,"E8");var subQ2=makeQuery(id+"F2.imprint","INTERSECT",VERTEX,{"derivedFrom":[subQ1,subQ0]});Q5=makeQuery(id+"F2.imprint","IMPRINT",FACE,{"disambiguationData":[TD([[makeQuery(id+"F2.imprint","IMPRINT",EDGE,{"disambiguationData":[TD([[subQ2,-1.0]])],"derivedFrom":subQ1}),1.0]])]});}
            var Q6;
            Q6=sQuery(id+"F2.wireOp",EDGE,"E8");
            revolve(context, id + "F13", {"entities" : qUnion([Q0, Q1, Q2, Q3, Q4, Q5]), "axis" : qUnion([Q6]), "revolveType" : RevolveType.FULL});
        }
        {
            var Q0;
            {var subQ0=sQuery(id+"F2.wireOp",EDGE,"E21.MirrorCS");var subQ5=sQuery(id+"F2.wireOp",EDGE,"E18.MirrorC");var subQ6=makeQuery(id+"F2.imprint","INTERSECT",VERTEX,{"derivedFrom":[subQ5,subQ0]});Q0=makeQuery(id+"F2.imprint","IMPRINT",FACE,{"disambiguationData":[TD([[makeQuery(id+"F2.imprint","IMPRINT",EDGE,{"disambiguationData":[TD([[subQ6,1.0]])],"derivedFrom":subQ5}),1.0]])]});}
            var Q1;
            {var subQ0=sQuery(id+"F2.wireOp",EDGE,"E21.MirrorCS");var subQ1=sQuery(id+"F2.wireOp",EDGE,"E18.MirrorC");var subQ2=makeQuery(id+"F2.imprint","INTERSECT",VERTEX,{"derivedFrom":[subQ1,subQ0]});Q1=makeQuery(id+"F2.imprint","IMPRINT",FACE,{"disambiguationData":[TD([[makeQuery(id+"F2.imprint","IMPRINT",EDGE,{"disambiguationData":[TD([[subQ2,1.0]])],"derivedFrom":subQ1}),-1.0]])]});}
            var Q2;
            {var subQ0=sQuery(id+"F2.wireOp",EDGE,"E20.MirrorCS");var subQ1=sQuery(id+"F2.wireOp",EDGE,"E18.MirrorC");var subQ2=makeQuery(id+"F2.imprint","INTERSECT",VERTEX,{"derivedFrom":[subQ1,subQ0]});Q2=makeQuery(id+"F2.imprint","IMPRINT",FACE,{"disambiguationData":[TD([[makeQuery(id+"F2.imprint","IMPRINT",EDGE,{"disambiguationData":[TD([[subQ2,-1.0]])],"derivedFrom":subQ1}),-1.0]])]});}
            var Q3;
            {var subQ0=sQuery(id+"F2.wireOp",EDGE,"E26.MirrorCS");var subQ1=sQuery(id+"F2.wireOp",EDGE,"E19.MirrorCS");var subQ2=makeQuery(id+"F2.imprint","INTERSECT",VERTEX,{"derivedFrom":[subQ1,subQ0]});Q3=makeQuery(id+"F2.imprint","IMPRINT",FACE,{"disambiguationData":[TD([[makeQuery(id+"F2.imprint","IMPRINT",EDGE,{"disambiguationData":[TD([[subQ2,-1.0]])],"derivedFrom":subQ1}),-1.0]])]});}
            var Q4;
            {var subQ1=sQuery(id+"F2.wireOp",EDGE,"E0.right");var subQ3=sQuery(id+"F2.wireOp",EDGE,"E19.MirrorCS");var subQ4=makeQuery(id+"F2.imprint","INTERSECT",VERTEX,{"derivedFrom":[subQ1,subQ3]});Q4=makeQuery(id+"F2.imprint","IMPRINT",FACE,{"disambiguationData":[TD([[makeQuery(id+"F2.imprint","IMPRINT",EDGE,{"disambiguationData":[TD([[subQ4,1.0]])],"derivedFrom":subQ3}),-1.0]])]});}
            var Q5;
            {var subQ0=sQuery(id+"F2.wireOp",EDGE,"E19.MirrorCS");var subQ1=sQuery(id+"F2.wireOp",EDGE,"E0.right");var subQ2=makeQuery(id+"F2.imprint","INTERSECT",VERTEX,{"derivedFrom":[subQ1,subQ0]});Q5=makeQuery(id+"F2.imprint","IMPRINT",FACE,{"disambiguationData":[TD([[makeQuery(id+"F2.imprint","IMPRINT",EDGE,{"disambiguationData":[TD([[subQ2,-1.0]])],"derivedFrom":subQ1}),1.0]])]});}
            var Q6;
            Q6=sQuery(id+"F2.wireOp",EDGE,"E21.MirrorCS");
            revolve(context, id + "F14", {"entities" : qUnion([Q0, Q1, Q2, Q3, Q4, Q5]), "axis" : qUnion([Q6]), "revolveType" : RevolveType.FULL});
        }
        {
            var Q0;
            Q0=makeQuery(id+"F14.opRevolve","SWEPT_EDGE",EDGE,{"disambiguationData":[OSD([sQuery(id+"F2.wireOp",EDGE,"E25.MirrorCS"),sQuery(id+"F2.wireOp",EDGE,"E28.MirrorCS")])]});
            var Q1;
            Q1=makeQuery(id+"F13.opRevolve","SWEPT_EDGE",EDGE,{"disambiguationData":[OSD([sQuery(id+"F2.wireOp",EDGE,"E24.bottom"),sQuery(id+"F2.wireOp",EDGE,"E27")])]});
            chamfer(context, id + "F15", {"entities" : qUnion([Q0, Q1]), "width" : (getVariable(context, 'E')) * mm, "tangentPropagation" : true});
        }
    });
